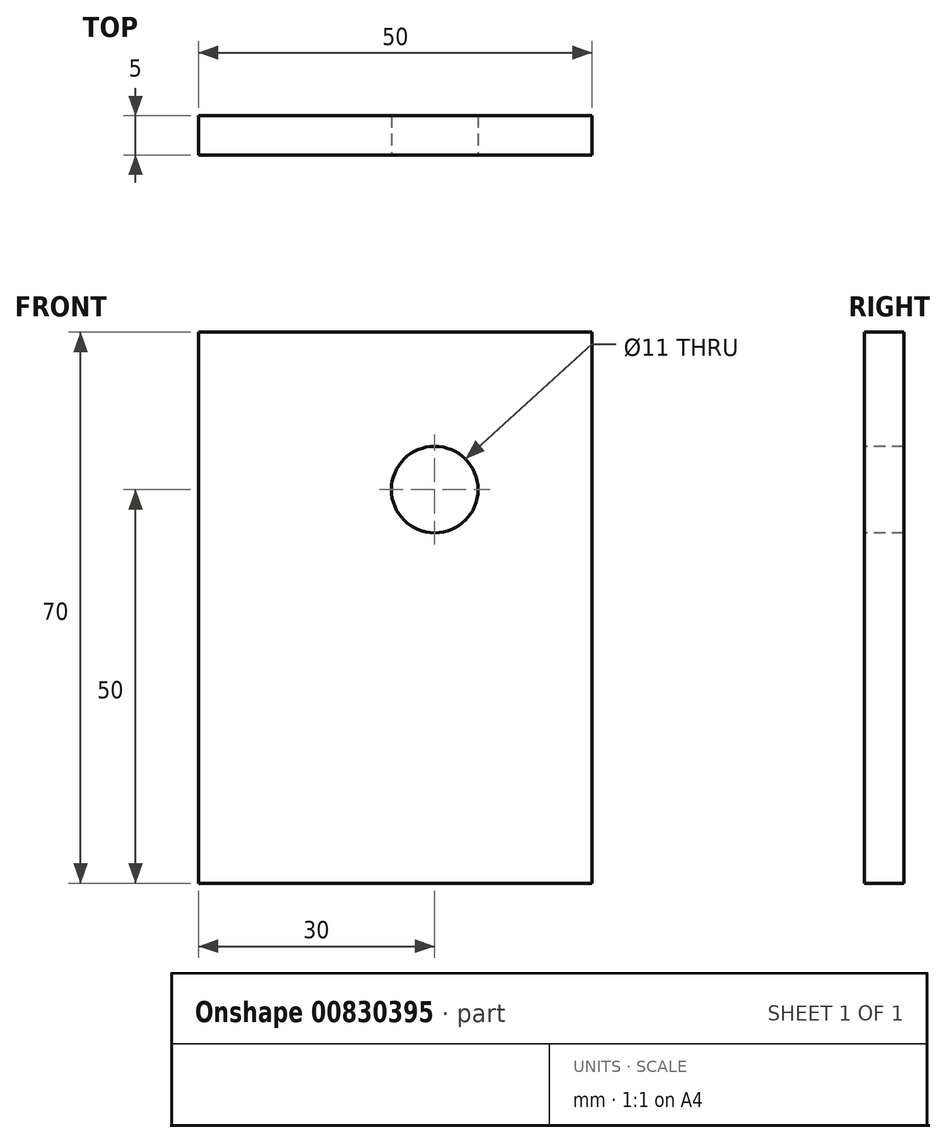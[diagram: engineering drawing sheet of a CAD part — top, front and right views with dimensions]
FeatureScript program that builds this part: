
annotation { "Feature Type Name" : "Feature", "Feature Type Description" : "" }
export const myFeature = defineFeature(function(context is Context, id is Id, definition is map)
    precondition{}
    {
        {
            var Q0;
            Q0=qCreatedBy(makeId("Front.planeOp"),FACE);
            var sketch = newSketch(context, id + "F0", { "sketchPlane" : qUnion([Q0])});
            skLineSegment(sketch, "E0.bottom", {"start": v(0, 0) * mm, "end": v(50, 0) * mm});
            skLineSegment(sketch, "E0.top", {"start": v(0, 70) * mm, "end": v(50, 70) * mm});
            skLineSegment(sketch, "E0.left", {"start": v(0, 0) * mm, "end": v(0, 70) * mm});
            skLineSegment(sketch, "E0.right", {"start": v(50, 0) * mm, "end": v(50, 70) * mm});
            skSolve(sketch);
        }
        {
            var Q0;
            Q0=qSketchRegion(id+"F0",true);
            extrude(context, id + "F1", {"entities" : qUnion([Q0]), "depth" : 5 * mm, "offsetDistance" : 25 * mm});
        }
        {
            var Q0;
            Q0=makeQuery(id+"F1.opExtrude","CAP_FACE",FACE,{"disambiguationData":[OSD([sQuery(id+"F0.wireOp",EDGE,"E0.bottom"),sQuery(id+"F0.wireOp",EDGE,"E0.top"),sQuery(id+"F0.wireOp",EDGE,"E0.left"),sQuery(id+"F0.wireOp",EDGE,"E0.right")])],"isStart":false});
            var sketch = newSketch(context, id + "F2", { "sketchPlane" : qUnion([Q0])});
            skPoint(sketch, "E1", {"position": v(30, 50) * mm});
            skSolve(sketch);
        }
        {
            var Q0;
            Q0=sQuery(id+"F2.wireOp",VERTEX,"E1");
            var Q1;
            Q1=makeQuery(id+"F1.opExtrude","SWEPT_BODY",BODY,{"disambiguationData":[OSD([sQuery(id+"F0.wireOp",EDGE,"E0.bottom"),sQuery(id+"F0.wireOp",EDGE,"E0.top"),sQuery(id+"F0.wireOp",EDGE,"E0.left"),sQuery(id+"F0.wireOp",EDGE,"E0.right")])]});
            hole(context, id + "F3", {"style" : HoleStyle.SIMPLE, "endStyle" : HoleEndStyle.THROUGH, "holeDiameter" : 11 * mm, "majorDiameter" : 5 * mm, "isTappedThrough" : true, "tappedDepth" : 12 * mm, "tapClearance" : 3, "locations" : qUnion([Q0]), "scope" : qUnion([Q1])});
        }
    });
